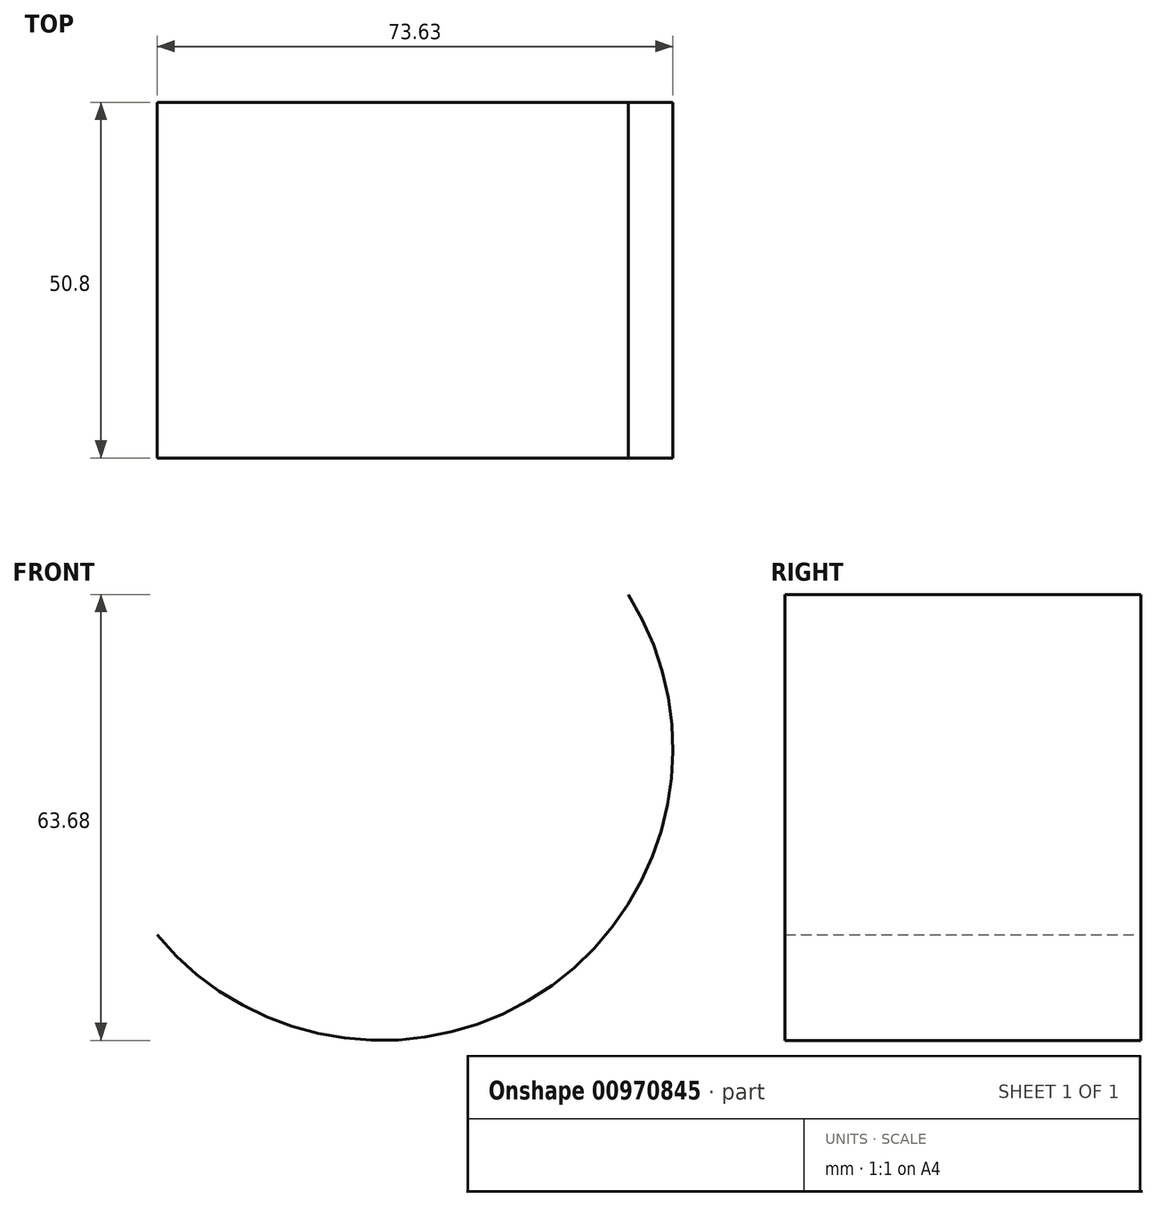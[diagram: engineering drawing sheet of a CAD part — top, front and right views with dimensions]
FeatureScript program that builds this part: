
annotation { "Feature Type Name" : "Feature", "Feature Type Description" : "" }
export const myFeature = defineFeature(function(context is Context, id is Id, definition is map)
    precondition{}
    {
        {
            var Q0;
            Q0=qCreatedBy(makeId("Front.planeOp"),FACE);
            var sketch = newSketch(context, id + "F0", { "sketchPlane" : qUnion([Q0])});
            skArc(sketch, "E0", {"start": v(0, 0) * mm, "mid": v(56.4, -7.19) * mm, "end": v(67.29, 48.61) * mm});
            skSolve(sketch);
        }
        {
            var Q0;
            Q0=sQuery(id+"F0.wireOp",EDGE,"E0");
            extrude(context, id + "F1", {"bodyType" : ToolBodyType.SURFACE, "surfaceEntities" : qUnion([Q0]), "endBound" : BoundingType.SYMMETRIC, "oppositeDirection" : true, "depth" : 50.8 * mm, "offsetDistance" : 25.4 * mm});
        }
    });
